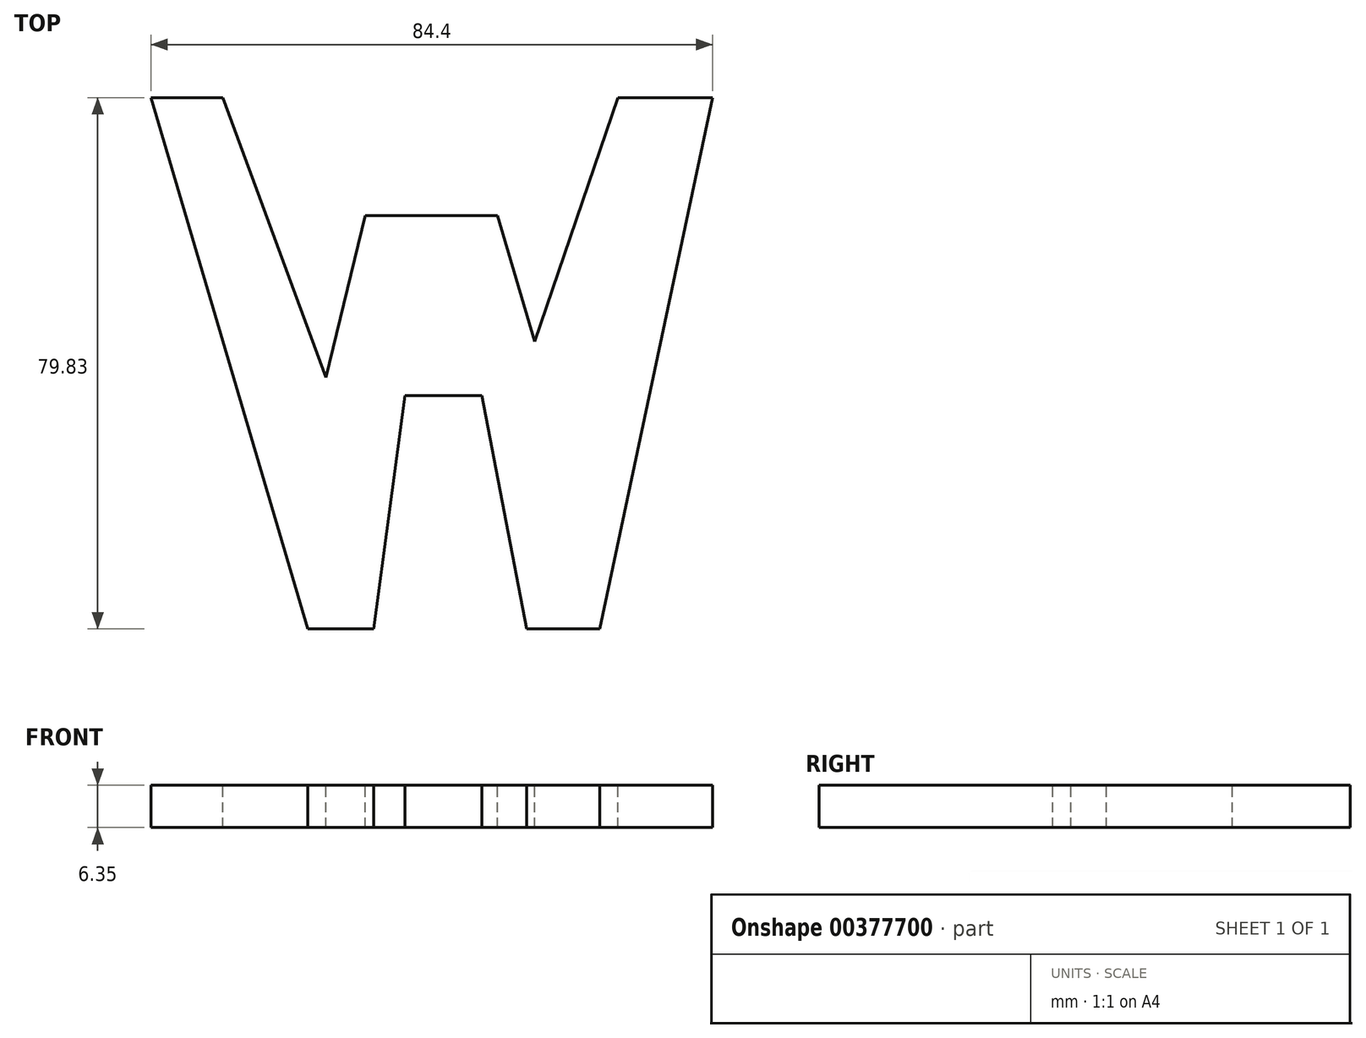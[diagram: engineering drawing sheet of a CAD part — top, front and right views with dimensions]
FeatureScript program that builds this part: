
annotation { "Feature Type Name" : "Feature", "Feature Type Description" : "" }
export const myFeature = defineFeature(function(context is Context, id is Id, definition is map)
    precondition{}
    {
        {
            var Q0;
            Q0=qCreatedBy(makeId("Top.planeOp"),FACE);
            var sketch = newSketch(context, id + "F0", { "sketchPlane" : qUnion([Q0])});
            skLineSegment(sketch, "E0.bottom", {"start": v(-41.11, 51.88) * mm, "end": v(43.3, 51.88) * mm});
            skLineSegment(sketch, "E0.top", {"start": v(-41.11, -27.95) * mm, "end": v(43.3, -27.95) * mm});
            skLineSegment(sketch, "E0.left", {"start": v(-41.11, 51.88) * mm, "end": v(-41.11, -27.95) * mm});
            skLineSegment(sketch, "E0.right", {"start": v(43.3, 51.88) * mm, "end": v(43.3, -27.95) * mm});
            skSolve(sketch);
        }
        {
            var Q0;
            Q0=makeQuery(id+"F0.imprint","IMPRINT",FACE,{"disambiguationData":[TD([[makeQuery(id+"F0.imprint","IMPRINT",EDGE,{"derivedFrom":sQuery(id+"F0.wireOp",EDGE,"E0.bottom")}),-1.0]])]});
            extrude(context, id + "F1", {"entities" : qUnion([Q0]), "depth" : 6.35 * mm});
        }
        {
            var Q0;
            Q0=makeQuery(id+"F1.opExtrude","CAP_FACE",FACE,{"disambiguationData":[OSD([sQuery(id+"F0.wireOp",EDGE,"E0.bottom"),sQuery(id+"F0.wireOp",EDGE,"E0.top"),sQuery(id+"F0.wireOp",EDGE,"E0.left"),sQuery(id+"F0.wireOp",EDGE,"E0.right")])],"isStart":false});
            var sketch = newSketch(context, id + "F2", { "sketchPlane" : qUnion([Q0])});
            skLineSegment(sketch, "E1", {"start": v(-41.11, 51.88) * mm, "end": v(-17.54, -27.95) * mm});
            skLineSegment(sketch, "E2", {"start": v(-7.67, -27.95) * mm, "end": v(-2.92, 7.12) * mm});
            skLineSegment(sketch, "E3", {"start": v(-2.92, 7.12) * mm, "end": v(8.59, 7.12) * mm});
            skLineSegment(sketch, "E4", {"start": v(8.59, 7.12) * mm, "end": v(15.34, -27.95) * mm});
            skLineSegment(sketch, "E5", {"start": v(26.3, -27.95) * mm, "end": v(43.3, 51.88) * mm});
            skLineSegment(sketch, "E6", {"start": v(43.3, 51.88) * mm, "end": v(-30.32, 51.88) * mm});
            skLineSegment(sketch, "E7", {"start": v(-30.32, 51.88) * mm, "end": v(-14.8, 9.86) * mm});
            skLineSegment(sketch, "E8", {"start": v(-14.8, 9.86) * mm, "end": v(-8.95, 34.16) * mm});
            skLineSegment(sketch, "E9", {"start": v(-8.95, 34.16) * mm, "end": v(10.96, 34.16) * mm});
            skLineSegment(sketch, "E10", {"start": v(10.96, 34.16) * mm, "end": v(16.55, 15.24) * mm});
            skLineSegment(sketch, "E11", {"start": v(16.55, 15.24) * mm, "end": v(29.04, 51.88) * mm});
            skSolve(sketch);
        }
        {
            var Q0;
            {var subQ0=sQuery(id+"F2.wireOp",EDGE,"E1");Q0=makeQuery(id+"F2.imprint","IMPRINT",FACE,{"disambiguationData":[TD([[makeQuery(id+"F2.imprint","IMPRINT",EDGE,{"derivedFrom":subQ0}),-1.0]])]});}
            var Q1;
            {var subQ0=sQuery(id+"F2.wireOp",EDGE,"E7");Q1=makeQuery(id+"F2.imprint","IMPRINT",FACE,{"disambiguationData":[TD([[makeQuery(id+"F2.imprint","IMPRINT",EDGE,{"derivedFrom":subQ0}),1.0]])]});}
            var Q2;
            {var subQ0=sQuery(id+"F2.wireOp",EDGE,"E5");Q2=makeQuery(id+"F2.imprint","IMPRINT",FACE,{"disambiguationData":[TD([[makeQuery(id+"F2.imprint","IMPRINT",EDGE,{"derivedFrom":subQ0}),-1.0]])]});}
            var Q3;
            {var subQ0=sQuery(id+"F2.wireOp",EDGE,"E2");Q3=makeQuery(id+"F2.imprint","IMPRINT",FACE,{"disambiguationData":[TD([[makeQuery(id+"F2.imprint","IMPRINT",EDGE,{"derivedFrom":subQ0}),-1.0]])]});}
            extrude(context, id + "F3", {"entities" : qUnion([Q0, Q1, Q2, Q3]), "operationType" : NewBodyOperationType.REMOVE, "oppositeDirection" : true, "depth" : 25.4 * mm});
        }
    });
